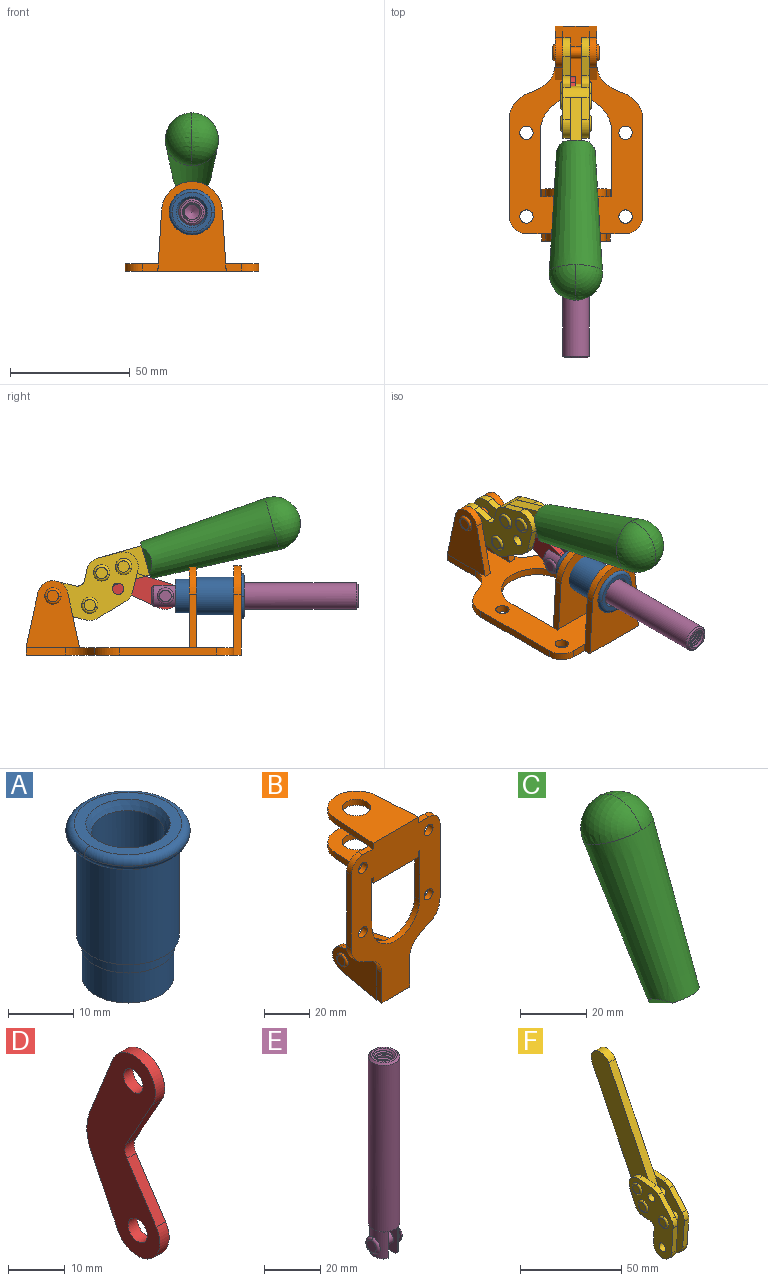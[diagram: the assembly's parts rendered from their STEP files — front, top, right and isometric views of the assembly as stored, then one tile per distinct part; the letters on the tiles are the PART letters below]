
ASSEMBLY  parts=6 mates=6
PART A: 15 faces, bbox 20.6x20.6x28.7 mm
  f0: torus R=8.26mm, axis (0,0,1), area 56.8mm2, adj f1,f10,f12
  f1: torus R=8.26mm, axis (0,0,1), area 56.8mm2, adj f0,f6,f13
  f2: cylinder r=5.59mm len=25.91mm, axis (0,0,1), area 909.6mm2, adj f3,f4
  f3: cone r=6.86mm half-angle=45deg, axis (0,0,-1), area 70.2mm2, adj f2,f14
  f4: cone r=6.47mm half-angle=30deg, axis (0,0,1), area 66.7mm2, adj f2,f13
  f5: cylinder r=7.04mm len=14.07mm, axis (0,0,1), area 252.6mm2, adj f11,f14
  f6: torus R=8.26mm, axis (0,0,1), area 56.8mm2, adj f1,f12,f13
  f7: cylinder r=7.16mm len=14.33mm, axis (0,0,1), area 91.5mm2, adj f9,f11
  f8: cylinder r=7.86mm len=18.42mm, axis (0,0,1), area 909.6mm2, adj f9,f10
  f9: plane 15.72x15.72mm, normal (0,0,-1), area 33mm2, adj f7,f8
  f10: plane 16.51x16.51mm, normal (0,0,-1), area 19.9mm2, adj f0,f8,f12
  f11: plane 14.33x14.33mm, normal (0,0,-1), area 5.7mm2, adj f5,f7
  f12: torus R=8.26mm, axis (0,0,1), area 56.8mm2, adj f0,f6,f10
  f13: plane 16.51x16.51mm, normal (0,0,1), area 82.7mm2, adj f1,f4,f6
  f14: plane 14.07x14.07mm, normal (0,0,-1), area 7.8mm2, adj f3,f5
PART B: 55 faces, bbox 55.7x37.4x89.8 mm
  f0: torus R=2.41mm, axis (-1,0,0), area 15mm2, adj f11,f15,f25
  f1: torus R=2.41mm, axis (-1,0,0), area 15mm2, adj f10,f12,f22
  f2: cylinder r=2.78mm len=5.56mm, axis (0,-1,0), area 54.2mm2, adj f30,f54
  f3: cylinder r=14.99mm len=29.97mm, axis (0,-1,0), area 145.9mm2, adj f30,f49,f53,f54
  f4: cylinder r=2.78mm len=5.56mm, axis (0,-1,0), area 54.2mm2, adj f30,f54
  f5: cylinder r=2.78mm len=5.56mm, axis (0,-1,0), area 54.2mm2, adj f30,f54
  f6: cylinder r=2.78mm len=5.56mm, axis (0,-1,0), area 54.2mm2, adj f30,f54
  f7: cylinder r=6.35mm len=12.7mm, axis (0,0,1), area 123.6mm2, adj f27,f51
  f8: cylinder r=6.35mm len=12.7mm, axis (0,0,-1), area 124.7mm2, adj f21,f35
  f9: cylinder r=2.41mm len=11.18mm, axis (-1,0,0), area 169.4mm2, adj f16,f19
  f10: plane 4.83x4.83mm, normal (1,0,0), area 18.3mm2, adj f1,f12
  f11: plane 4.83x4.83mm, normal (-1,0,0), area 18.3mm2, adj f0,f15
  f12: torus R=2.41mm, axis (-1,0,0), area 15mm2, adj f1,f10,f22
  f13: cylinder r=6.35mm len=12.41mm, axis (1,0,0), area 53.4mm2, adj f18,f19,f22,f23
  f14: cylinder r=6.35mm len=12.41mm, axis (-1,0,0), area 53.4mm2, adj f16,f17,f24,f25
  f15: torus R=2.41mm, axis (-1,0,0), area 15mm2, adj f0,f11,f25
  f16: plane 27.86x22.35mm, normal (1,0,0), area 425.4mm2, adj f9,f14,f17,f24,f30
  f17: plane 22.86x4.97mm, normal (0,0.21,0.98), area 72.5mm2, adj f14,f16,f25,f30
  f18: plane 22.86x4.97mm, normal (0,0.21,0.98), area 72.5mm2, adj f13,f19,f22,f30
  f19: plane 27.86x22.35mm, normal (-1,0,0), area 425.4mm2, adj f9,f13,f18,f23,f30
  f20: cylinder r=12.7mm len=25.35mm, axis (0,0,-1), area 119.8mm2, adj f21,f34,f35,f36
  f21: plane 34.21x28.07mm, normal (0,0,-1), area 702.4mm2, adj f8,f20,f30,f34,f36
  f22: plane 27.96x22.45mm, normal (1,0,0), area 407.2mm2, adj f1,f12,f13,f18,f23,f30,f42,f43
  f23: plane 22.86x4.97mm, normal (0,0.21,-0.98), area 72.5mm2, adj f13,f19,f22,f44
  f24: plane 22.86x4.97mm, normal (0,0.21,-0.98), area 72.5mm2, adj f14,f16,f25,f44
  f25: plane 27.86x22.35mm, normal (-1,0,0), area 407.1mm2, adj f0,f14,f15,f17,f24,f30,f45,f46
  f26: plane 3.1x0.95mm, normal (0,0,-1), area 2.7mm2, adj f30,f49,f50,f54
  f27: plane 34.21x28.07mm, normal (0,0,1), area 702.4mm2, adj f7,f28,f30,f50,f52
  f28: cylinder r=12.7mm len=25.35mm, axis (0,0,1), area 118.8mm2, adj f27,f50,f51,f52
  f29: plane 3.1x0.95mm, normal (0,0,-1), area 2.7mm2, adj f30,f52,f53,f54
  f30: plane 86.54x55.63mm, normal (0,1,0), area 2362.9mm2, adj f2,f3,f4,f5,f6,f16,f17,f18
  f31: plane 40.56x3.1mm, normal (-1,0,0), area 125.7mm2, adj f30,f32,f48,f54
  f32: cylinder r=7.11mm len=7.11mm, axis (0,-1,0), area 34.6mm2, adj f30,f31,f33,f54
  f33: plane 6.67x3.1mm, normal (0,0,1), area 20.4mm2, adj f30,f32,f34,f54
  f34: plane 25.39x3.13mm, normal (-1,0.06,0), area 79.5mm2, adj f20,f21,f33,f35,f54
  f35: plane 37.31x28.45mm, normal (0,0,1), area 789.9mm2, adj f8,f20,f34,f36,f54
  f36: plane 25.39x3.13mm, normal (1,0.06,0), area 79.5mm2, adj f20,f21,f35,f37,f54
  f37: plane 6.67x3.1mm, normal (0,0,1), area 20.4mm2, adj f30,f36,f38,f54
  f38: cylinder r=7.11mm len=7.11mm, axis (0,-1,0), area 34.6mm2, adj f30,f37,f39,f54
  f39: plane 40.56x3.1mm, normal (1,0,0), area 125.7mm2, adj f30,f38,f40,f54
  f40: cylinder r=11.18mm len=10.16mm, axis (0,-1,0), area 39.5mm2, adj f30,f39,f41,f54
  f41: plane 6.09x3.1mm, normal (0.42,0,-0.91), area 20.8mm2, adj f30,f40,f42,f54
  f42: cylinder r=11.18mm len=9.41mm, axis (0,-1,0), area 37.2mm2, adj f22,f30,f41,f43,f54
  f43: plane 16.5x3.1mm, normal (1,0,0), area 51.1mm2, adj f22,f42,f44,f54
  f44: plane 17.37x3.1mm, normal (0,0,-1), area 53.8mm2, adj f23,f24,f30,f43,f45,f54
  f45: plane 16.5x3.1mm, normal (-1,0,0), area 51.1mm2, adj f25,f44,f46,f54
  f46: cylinder r=11.18mm len=9.41mm, axis (0,-1,0), area 37.2mm2, adj f25,f30,f45,f47,f54
  f47: plane 6.09x3.1mm, normal (-0.42,0,-0.91), area 20.8mm2, adj f30,f46,f48,f54
  f48: cylinder r=11.18mm len=10.16mm, axis (0,-1,0), area 39.5mm2, adj f30,f31,f47,f54
  f49: plane 26.54x3.1mm, normal (-1,0,0), area 82.3mm2, adj f3,f26,f30,f54
  f50: plane 25.39x3.1mm, normal (1,0.06,0), area 78.8mm2, adj f26,f27,f28,f51,f54
  f51: plane 37.31x28.45mm, normal (0,0,-1), area 789.9mm2, adj f7,f28,f50,f52,f54
  f52: plane 25.39x3.1mm, normal (-1,0.06,0), area 78.8mm2, adj f27,f28,f29,f51,f54
  f53: plane 26.54x3.1mm, normal (1,0,0), area 82.3mm2, adj f3,f29,f30,f54
  f54: plane 89.66x55.63mm, normal (0,-1,0), area 2678.5mm2, adj f2,f3,f4,f5,f6,f26,f29,f31
PART C: 11 faces, bbox 22.3x42.6x64.5 mm
  f0: sphere r=11.13mm, area 411.4mm2, adj f1,f8
  f1: cone r=11.11mm half-angle=3.3deg, axis (0,0.44,0.9), area 3251.8mm2, adj f0,f7,f8,f9,f10
  f2: cylinder r=6.16mm len=11.7mm, axis (1,0,0), area 89.5mm2, adj f3,f4,f5,f6
  f3: plane 60.23x36.75mm, normal (-1,0,0), area 763.6mm2, adj f2,f4,f6,f10
  f4: plane 51.37x25.05mm, normal (0,0.9,-0.44), area 264.2mm2, adj f2,f3,f5,f10
  f5: plane 60.23x36.75mm, normal (1,0,0), area 763.6mm2, adj f2,f4,f6,f10
  f6: plane 51.37x25.05mm, normal (0,-0.9,0.44), area 264.2mm2, adj f2,f3,f5,f10
  f7: plane 9.95x5.95mm, normal (0.71,-0.31,-0.64), area 25.8mm2, adj f1,f10
  f8: sphere r=11.13mm, area 411.4mm2, adj f0,f1
  f9: plane 9.95x5.95mm, normal (-0.71,-0.31,-0.64), area 25.8mm2, adj f1,f10
  f10: plane 14.27x11.38mm, normal (0,-0.44,-0.9), area 106.7mm2, adj f1,f3,f4,f5,f6,f7,f9
PART D: 12 faces, bbox 2.3x18.2x42.8 mm
  f0: cylinder r=2.4mm len=4.8mm, axis (1,0,0), area 34.9mm2, adj f4,f11
  f1: cylinder r=10.41mm len=8.47mm, axis (1,0,0), area 20.2mm2, adj f4,f9,f10,f11
  f2: cylinder r=3.05mm len=3.16mm, axis (1,0,0), area 7.7mm2, adj f4,f6,f7,f11
  f3: cylinder r=2.4mm len=4.8mm, axis (1,0,0), area 34.9mm2, adj f4,f11
  f4: plane 42.81x18.23mm, normal (-1,0,0), area 414.1mm2, adj f0,f1,f2,f3,f5,f6,f7,f8
  f5: cylinder r=5.54mm len=10.67mm, axis (1,0,0), area 41.8mm2, adj f4,f6,f10,f11
  f6: plane 11.66x6.53mm, normal (0,-0.87,-0.49), area 30.9mm2, adj f2,f4,f5,f11
  f7: plane 11.17x7.33mm, normal (0,-0.84,0.55), area 30.9mm2, adj f2,f4,f8,f11
  f8: cylinder r=5.54mm len=10.51mm, axis (1,0,0), area 41.8mm2, adj f4,f7,f9,f11
  f9: plane 13.67x6.67mm, normal (0,0.9,-0.44), area 35.1mm2, adj f1,f4,f8,f11
  f10: plane 14.1x5.7mm, normal (0,0.93,0.37), area 35.1mm2, adj f1,f4,f5,f11
  f11: plane 42.81x18.23mm, normal (1,0,0), area 414.1mm2, adj f0,f1,f2,f3,f5,f6,f7,f8
PART E: 48 faces, bbox 12.6x11.1x86.1 mm
  f0: torus R=2.41mm, axis (-1,0,0), area 15mm2, adj f30,f32,f34
  f1: torus R=2.41mm, axis (-1,0,0), area 15mm2, adj f29,f31,f33
  f2: cylinder r=5.54mm len=72.39mm, axis (0,0,1), area 2518.5mm2, adj f3,f4,f42,f43
  f3: cone r=5.54mm half-angle=45deg, axis (0,0,1), area 7.6mm2, adj f2,f5,f41
  f4: cone r=5.54mm half-angle=45deg, axis (0,0,-1), area 34.9mm2, adj f2,f39
  f5: cylinder r=5.08mm len=11.48mm, axis (0,0,1), area 108.3mm2, adj f3,f7,f8,f41
  f6: cylinder r=2.41mm len=4.83mm, axis (-1,0,0), area 71.2mm2, adj f40,f41
  f7: cylinder r=2.41mm len=4.83mm, axis (-1,0,0), area 7.6mm2, adj f5,f34
  f8: cone r=5.08mm half-angle=45deg, axis (0,0,1), area 10.6mm2, adj f5,f37,f41
  f9: cone r=3.98mm half-angle=45deg, axis (0,0,1), area 17.6mm2, adj f27,f39,f45,f46,f47
  f10: cylinder r=2.41mm len=4.83mm, axis (-1,0,0), area 7.6mm2, adj f33,f38
  f11: cylinder r=3.2mm len=6.4mm, axis (0,0,1), area 78.4mm2, adj f12,f28,f44,f45,f47
  f12: cylinder r=3.2mm len=6.4mm, axis (0,0,1), area 10.5mm2, adj f11,f13,f45,f47
  f13: cylinder r=3.2mm len=6.4mm, axis (0,0,1), area 10.5mm2, adj f12,f14,f45,f47
  f14: cylinder r=3.2mm len=6.4mm, axis (0,0,1), area 10.5mm2, adj f13,f15,f45,f47
  f15: cylinder r=3.2mm len=6.4mm, axis (0,0,1), area 10.5mm2, adj f14,f16,f45,f47
  f16: cylinder r=3.2mm len=6.4mm, axis (0,0,1), area 10.5mm2, adj f15,f17,f45,f47
  f17: cylinder r=3.2mm len=6.4mm, axis (0,0,1), area 10.5mm2, adj f16,f18,f45,f47
  f18: cylinder r=3.2mm len=6.4mm, axis (0,0,1), area 10.5mm2, adj f17,f19,f45,f47
  f19: cylinder r=3.2mm len=6.4mm, axis (0,0,1), area 10.5mm2, adj f18,f20,f45,f47
  f20: cylinder r=3.2mm len=6.4mm, axis (0,0,1), area 10.5mm2, adj f19,f21,f45,f47
  f21: cylinder r=3.2mm len=6.4mm, axis (0,0,1), area 10.5mm2, adj f20,f22,f45,f47
  f22: cylinder r=3.2mm len=6.4mm, axis (0,0,1), area 10.5mm2, adj f21,f23,f45,f47
  f23: cylinder r=3.2mm len=6.4mm, axis (0,0,1), area 10.5mm2, adj f22,f24,f45,f47
  f24: cylinder r=3.2mm len=6.4mm, axis (0,0,1), area 10.5mm2, adj f23,f25,f45,f47
  f25: cylinder r=3.2mm len=6.4mm, axis (0,0,1), area 10.5mm2, adj f24,f26,f45,f47
  f26: cylinder r=3.2mm len=6.4mm, axis (0,0,1), area 10.5mm2, adj f25,f27,f45,f47
  f27: cylinder r=3.2mm len=6.4mm, axis (0,0,1), area 7.4mm2, adj f9,f26,f45,f47
  f28: cone r=3.2mm half-angle=60deg, axis (0,0,1), area 37.2mm2, adj f11
  f29: plane 4.83x4.83mm, normal (-1,0,0), area 18.3mm2, adj f1,f31
  f30: plane 4.83x4.83mm, normal (1,0,0), area 18.3mm2, adj f0,f32
  f31: torus R=2.41mm, axis (-1,0,0), area 15mm2, adj f1,f29,f33
  f32: torus R=2.41mm, axis (-1,0,0), area 15mm2, adj f0,f30,f34
  f33: plane 6.83x6.83mm, normal (1,0,0), area 18.3mm2, adj f1,f10,f31
  f34: plane 6.83x6.83mm, normal (-1,0,0), area 18.3mm2, adj f0,f7,f32
  f35: cone r=5.08mm half-angle=45deg, axis (0,0,1), area 10.6mm2, adj f36,f38,f40
  f36: plane 7.25x1.97mm, normal (0,0,-1), area 10mm2, adj f35,f40
  f37: plane 7.25x1.97mm, normal (0,0,-1), area 10mm2, adj f8,f41
  f38: cylinder r=5.08mm len=11.48mm, axis (0,0,1), area 108.3mm2, adj f10,f35,f40,f42
  f39: plane 9.55x9.55mm, normal (0,0,1), area 22mm2, adj f4,f9
  f40: plane 12.76x10.09mm, normal (1,0,0), area 95.7mm2, adj f6,f35,f36,f38,f42,f43
  f41: plane 12.76x10.09mm, normal (-1,0,0), area 95.7mm2, adj f3,f5,f6,f8,f37,f43
  f42: cone r=5.54mm half-angle=45deg, axis (0,0,1), area 7.6mm2, adj f2,f38,f40
  f43: plane 11.07x4.7mm, normal (0,0,-1), area 50.4mm2, adj f2,f40,f41
  f44: plane 0.89x0.62mm, normal (-1,0,0), area 0.3mm2, adj f11,f45,f46,f47
  f45: bspline ~24.8x7.63mm, area 266.6mm2, adj f9,f11,f12,f13,f14,f15,f16,f17
  f46: bspline ~24.87x7.63mm, area 73.6mm2, adj f9,f44,f45,f47
  f47: bspline ~24.98x7.63mm, area 272.5mm2, adj f9,f11,f12,f13,f14,f15,f16,f17
PART F: 59 faces, bbox 12.9x60.2x99.6 mm
  f0: torus R=2.39mm, axis (-1,0,0), area 14.9mm2, adj f20,f43,f51
  f1: torus R=2.39mm, axis (-1,0,0), area 14.9mm2, adj f19,f42,f51
  f2: torus R=2.39mm, axis (-1,0,0), area 14.9mm2, adj f18,f35,f51
  f3: torus R=2.39mm, axis (-1,0,0), area 14.9mm2, adj f14,f17,f23
  f4: torus R=2.39mm, axis (-1,0,0), area 14.9mm2, adj f13,f16,f23
  f5: torus R=2.39mm, axis (-1,0,0), area 14.9mm2, adj f12,f15,f23
  f6: cylinder r=2.39mm len=4.78mm, axis (1,0,0), area 46.5mm2, adj f48,f50,f51
  f7: cylinder r=2.39mm len=4.78mm, axis (1,0,0), area 46.5mm2, adj f50,f51
  f8: cylinder r=6.35mm len=12.68mm, axis (1,0,0), area 61.8mm2, adj f38,f39,f50,f51
  f9: cylinder r=2.39mm len=4.78mm, axis (-1,0,0), area 70.5mm2, adj f46,f50
  f10: cylinder r=2.39mm len=4.78mm, axis (-1,0,0), area 46.5mm2, adj f23,f45,f46
  f11: cylinder r=2.39mm len=4.78mm, axis (-1,0,0), area 46.5mm2, adj f23,f46
  f12: plane 4.78x4.78mm, normal (1,0,0), area 17.9mm2, adj f5,f15
  f13: plane 4.78x4.78mm, normal (1,0,0), area 17.9mm2, adj f4,f16
  f14: plane 4.78x4.78mm, normal (1,0,0), area 17.9mm2, adj f3,f17
  f15: torus R=2.39mm, axis (-1,0,0), area 14.9mm2, adj f5,f12,f23
  f16: torus R=2.39mm, axis (-1,0,0), area 14.9mm2, adj f4,f13,f23
  f17: torus R=2.39mm, axis (-1,0,0), area 14.9mm2, adj f3,f14,f23
  f18: plane 4.78x4.78mm, normal (-1,0,0), area 17.9mm2, adj f2,f35
  f19: plane 4.78x4.78mm, normal (-1,0,0), area 17.9mm2, adj f1,f42
  f20: plane 4.78x4.78mm, normal (-1,0,0), area 17.9mm2, adj f0,f43
  f21: plane 2.26x0.2mm, normal (1,0,0), area 0.2mm2, adj f31,f44
  f22: plane 2.26x0.2mm, normal (-1,0,0), area 0.2mm2, adj f41,f44
  f23: plane 39.37x30.77mm, normal (1,0,0), area 565.5mm2, adj f3,f4,f5,f10,f11,f15,f16,f17
  f24: cylinder r=6.1mm len=4.15mm, axis (-1,0,0), area 14.7mm2, adj f23,f25,f32,f46
  f25: plane 10.25x9.01mm, normal (0,-0.75,0.66), area 42.3mm2, adj f23,f24,f26,f46
  f26: cylinder r=6.35mm len=4.64mm, axis (-1,0,0), area 15.6mm2, adj f23,f25,f27,f46
  f27: plane 15.84x3.1mm, normal (0,-1,-0.07), area 49.2mm2, adj f23,f26,f28,f46
  f28: cylinder r=6.35mm len=12.68mm, axis (-1,0,0), area 61.8mm2, adj f23,f27,f29,f46
  f29: plane 8.11x3.1mm, normal (0,1,0.07), area 25.2mm2, adj f23,f28,f30,f46
  f30: cylinder r=3.05mm len=3.25mm, axis (-1,0,0), area 14.8mm2, adj f23,f29,f31,f46
  f31: plane 5.99x3.1mm, normal (0,0.07,-1), area 18.6mm2, adj f21,f23,f30,f44,f46
  f32: plane 9.5x3.1mm, normal (0,-0.07,1), area 29.5mm2, adj f23,f24,f33,f46,f47
  f33: cylinder r=6.1mm len=8.63mm, axis (-1,0,0), area 39.1mm2, adj f23,f32,f34,f47
  f34: plane 8.65x3.96mm, normal (0,0.91,-0.42), area 29.5mm2, adj f23,f33,f44,f47
  f35: torus R=2.39mm, axis (-1,0,0), area 14.9mm2, adj f2,f18,f51
  f36: plane 10.25x9.01mm, normal (0,-0.75,0.66), area 42.3mm2, adj f37,f49,f50,f51
  f37: cylinder r=6.35mm len=4.64mm, axis (1,0,0), area 15.6mm2, adj f36,f38,f50,f51
  f38: plane 15.84x3.1mm, normal (0,-1,-0.07), area 49.2mm2, adj f8,f37,f50,f51
  f39: plane 8.11x3.1mm, normal (0,1,0.07), area 25.2mm2, adj f8,f40,f50,f51
  f40: cylinder r=3.05mm len=3.25mm, axis (1,0,0), area 14.8mm2, adj f39,f41,f50,f51
  f41: plane 5.99x3.1mm, normal (0,0.07,-1), area 18.6mm2, adj f22,f40,f44,f50,f51
  f42: torus R=2.39mm, axis (-1,0,0), area 14.9mm2, adj f1,f19,f51
  f43: torus R=2.39mm, axis (-1,0,0), area 14.9mm2, adj f0,f20,f51
  f44: cylinder r=6.35mm len=12.12mm, axis (-1,0,0), area 128.9mm2, adj f21,f22,f23,f31,f34,f41,f46,f47
  f45: plane 2.65x1.35mm, normal (1,0,0), area 1mm2, adj f10,f55
  f46: plane 39.08x20.42mm, normal (-1,0,0), area 412.5mm2, adj f9,f10,f11,f24,f25,f26,f27,f28
  f47: plane 77.62x39.82mm, normal (1,0,0), area 850mm2, adj f32,f33,f34,f44,f53,f54,f55
  f48: plane 2.65x1.35mm, normal (-1,0,0), area 1mm2, adj f6,f55
  f49: cylinder r=6.1mm len=4.15mm, axis (1,0,0), area 14.7mm2, adj f36,f50,f51,f56
  f50: plane 39.08x20.42mm, normal (1,0,0), area 412.5mm2, adj f6,f7,f8,f9,f36,f37,f38,f39
  f51: plane 39.37x30.77mm, normal (-1,0,0), area 565.5mm2, adj f0,f1,f2,f6,f7,f8,f35,f36
  f52: plane 8.65x3.96mm, normal (0,0.91,-0.42), area 29.5mm2, adj f44,f51,f57,f58
  f53: plane 68.49x33.4mm, normal (0,0.9,-0.44), area 358.1mm2, adj f44,f47,f54,f58
  f54: cylinder r=6.35mm len=12.06mm, axis (1,0,0), area 93.7mm2, adj f47,f53,f55,f58
  f55: plane 68.49x33.4mm, normal (0,-0.9,0.44), area 358.1mm2, adj f44,f45,f46,f47,f48,f50,f54,f58
  f56: plane 9.5x3.1mm, normal (0,-0.07,1), area 29.5mm2, adj f49,f50,f51,f57,f58
  f57: cylinder r=6.1mm len=8.63mm, axis (1,0,0), area 39.1mm2, adj f51,f52,f56,f58
  f58: plane 77.62x39.82mm, normal (-1,0,0), area 850mm2, adj f44,f52,f53,f54,f55,f56,f57
PLACE A rot(axis=(1,0,0),90deg) t=(0,10.41,0)mm
PLACE B rot(axis=(1,0,0),90deg) t=(0,9.14,0)mm fixed
PLACE C rot(axis=(1,0,0),100deg) t=(-0.04,13.9,-5.2)mm
PLACE D rot(axis=(1,0,0),85.1deg) t=(-1.16,7.61,-1.24)mm
PLACE E rot(axis=(1,0,0),90deg) t=(0,9.79,0)mm
PLACE F rot(axis=(1,0,0),100deg) t=(0,13.9,-5.2)mm
MATE revolute F.f7 <-> B.f0  axis (-1,0,0) through (0,41.23,24.61)mm
MATE slider E.f2 <-> B.f7  axis (0,-1,0) through (0,-48.99,24.61)mm
MATE revolute D.f3 <-> F.f4  axis (1,0,0) through (0,25.83,20.77)mm
MATE fastened A.f2 <-> B.f7  axis (0,-1,0) through (0,-37.25,24.61)mm
MATE fastened C.f2 <-> F.f54  axis (1,0,0) through (-2.35,-52.38,55.25)mm
MATE revolute D.f5 <-> E.f6  axis (1,0,0) through (0,-5.69,24.61)mm
